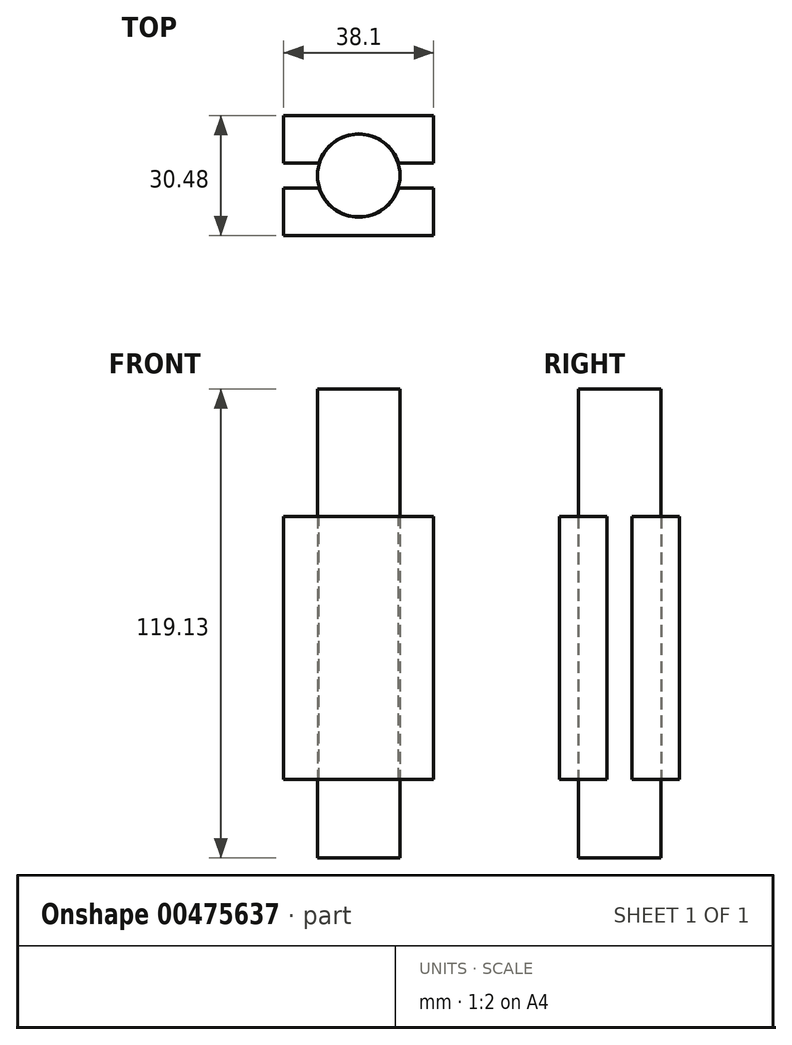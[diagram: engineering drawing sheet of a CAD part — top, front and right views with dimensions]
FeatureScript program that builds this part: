
annotation { "Feature Type Name" : "Feature", "Feature Type Description" : "" }
export const myFeature = defineFeature(function(context is Context, id is Id, definition is map)
    precondition{}
    {
        {
            var Q0;
            Q0=qCreatedBy(makeId("Top.planeOp"),FACE);
            var sketch = newSketch(context, id + "F0", { "sketchPlane" : qUnion([Q0])});
            skCircle(sketch, "E0", {"center": v(0, 0) * mm, "radius": 10.48 * mm});
            skSolve(sketch);
        }
        {
            var Q0;
            Q0=makeQuery(id+"F0.imprint","IMPRINT",FACE,{"disambiguationData":[TD([[makeQuery(id+"F0.imprint","IMPRINT",EDGE,{"derivedFrom":sQuery(id+"F0.wireOp",EDGE,"E0")}),1.0]])]});
            extrude(context, id + "F1", {"entities" : qUnion([Q0]), "depth" : 119.13 * mm});
        }
        {
            var Q0;
            Q0=qCreatedBy(makeId("Front.planeOp"),FACE);
            var sketch = newSketch(context, id + "F2", { "sketchPlane" : qUnion([Q0])});
            skLineSegment(sketch, "E1.bottom", {"start": v(19.05, 19.93) * mm, "end": v(-19.05, 19.93) * mm});
            skLineSegment(sketch, "E1.top", {"start": v(19.05, 86.75) * mm, "end": v(-19.05, 86.75) * mm});
            skLineSegment(sketch, "E1.left", {"start": v(19.05, 19.93) * mm, "end": v(19.05, 86.75) * mm});
            skLineSegment(sketch, "E1.right", {"start": v(-19.05, 19.93) * mm, "end": v(-19.05, 86.75) * mm});
            skPoint(sketch, "E1.middle", {"position": v(0, 53.34) * mm});
            skSolve(sketch);
        }
        {
            var Q0;
            Q0=makeQuery(id+"F2.imprint","IMPRINT",FACE,{"disambiguationData":[TD([[makeQuery(id+"F2.imprint","IMPRINT",EDGE,{"derivedFrom":sQuery(id+"F2.wireOp",EDGE,"E1.bottom")}),-1.0]])]});
            extrude(context, id + "F3", {"entities" : qUnion([Q0]), "depth" : 15.24 * mm, "hasSecondDirection" : true, "secondDirectionOppositeDirection" : true, "secondDirectionDepth" : 15.24 * mm});
        }
        {
            var Q0;
            Q0=makeQuery(id+"F1.opExtrude","SWEPT_BODY",BODY,{"disambiguationData":[OSD([sQuery(id+"F0.wireOp",EDGE,"E0")])]});
            var Q1;
            Q1=makeQuery(id+"F3.opExtrude","SWEPT_BODY",BODY,{"disambiguationData":[OSD([sQuery(id+"F2.wireOp",EDGE,"E1.bottom"),sQuery(id+"F2.wireOp",EDGE,"E1.top"),sQuery(id+"F2.wireOp",EDGE,"E1.left"),sQuery(id+"F2.wireOp",EDGE,"E1.right")])]});
            var Q2;
            Q2=makeQuery(id+"F1.opExtrude","SWEPT_FACE",FACE,{"disambiguationData":[OSD([sQuery(id+"F0.wireOp",EDGE,"E0")])]});
            booleanBodies(context, id + "F4", {"operationType" : BooleanOperationType.SUBTRACTION, "tools" : qUnion([Q0]), "targets" : qUnion([Q1]), "offset" : true, "entitiesToOffset" : qUnion([Q2]), "offsetDistance" : 0.13 * mm, "keepTools" : true});
        }
        {
            var Q0;
            Q0=makeQuery(id+"F3.opExtrude","SWEPT_FACE",FACE,{"disambiguationData":[OSD([sQuery(id+"F2.wireOp",EDGE,"E1.top")])]});
            var sketch = newSketch(context, id + "F5", { "sketchPlane" : qUnion([Q0])});
            skLineSegment(sketch, "E2.bottom", {"start": v(-19.05, 3.18) * mm, "end": v(19.05, 3.18) * mm});
            skLineSegment(sketch, "E2.top", {"start": v(-19.05, -3.18) * mm, "end": v(19.05, -3.18) * mm});
            skLineSegment(sketch, "E2.left", {"start": v(-19.05, 3.18) * mm, "end": v(-19.05, -3.18) * mm});
            skLineSegment(sketch, "E2.right", {"start": v(19.05, 3.18) * mm, "end": v(19.05, -3.18) * mm});
            skPoint(sketch, "E2.middle", {"position": v(0, 0) * mm});
            skSolve(sketch);
        }
        {
            var Q0;
            {var subQ0=sQuery(id+"F5.wireOp",EDGE,"E2.left");Q0=makeQuery(id+"F5.imprint","IMPRINT",FACE,{"disambiguationData":[TD([[makeQuery(id+"F5.imprint","IMPRINT",EDGE,{"derivedFrom":subQ0}),-1.0]])]});}
            var Q1;
            {var subQ0=sQuery(id+"F5.wireOp",EDGE,"E2.right");Q1=makeQuery(id+"F5.imprint","IMPRINT",FACE,{"disambiguationData":[TD([[makeQuery(id+"F5.imprint","IMPRINT",EDGE,{"derivedFrom":subQ0}),1.0]])]});}
            extrude(context, id + "F6", {"entities" : qUnion([Q0, Q1]), "operationType" : NewBodyOperationType.REMOVE, "endBound" : BoundingType.THROUGH_ALL, "oppositeDirection" : true, "depth" : 25.4 * mm});
        }
    });
